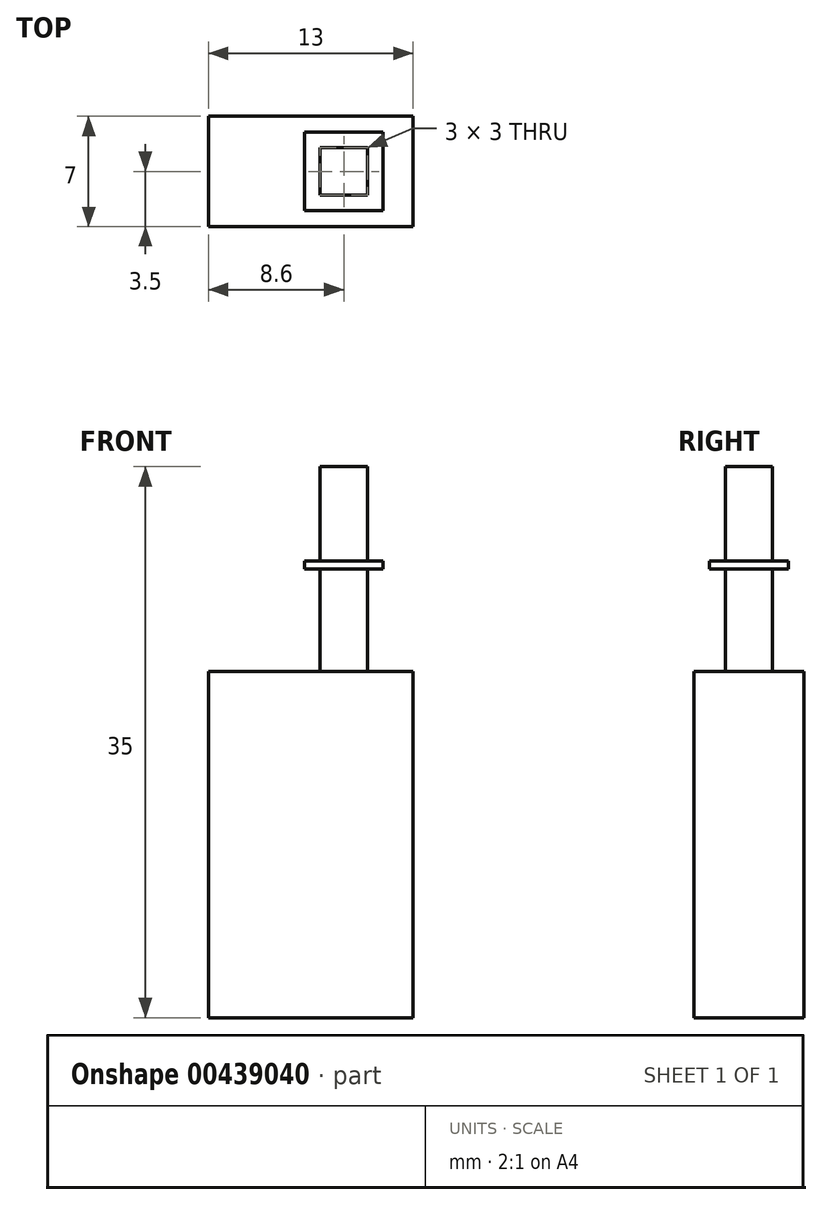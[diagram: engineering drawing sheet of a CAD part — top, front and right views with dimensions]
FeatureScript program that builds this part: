
annotation { "Feature Type Name" : "Feature", "Feature Type Description" : "" }
export const myFeature = defineFeature(function(context is Context, id is Id, definition is map)
    precondition{}
    {
        {
            var Q0;
            Q0=qCreatedBy(makeId("Top.planeOp"),FACE);
            var sketch = newSketch(context, id + "F0", { "sketchPlane" : qUnion([Q0])});
            skLineSegment(sketch, "E0.bottom", {"start": v(6.5, -3.5) * mm, "end": v(-6.5, -3.5) * mm});
            skLineSegment(sketch, "E0.top", {"start": v(6.5, 3.5) * mm, "end": v(-6.5, 3.5) * mm});
            skLineSegment(sketch, "E0.left", {"start": v(6.5, -3.5) * mm, "end": v(6.5, 3.5) * mm});
            skLineSegment(sketch, "E0.right", {"start": v(-6.5, -3.5) * mm, "end": v(-6.5, 3.5) * mm});
            skPoint(sketch, "E0.middle", {"position": v(0, 0) * mm});
            skSolve(sketch);
        }
        {
            var Q0;
            Q0=qSketchRegion(id+"F0",true);
            extrude(context, id + "F1", {"entities" : qUnion([Q0]), "depth" : 22 * mm});
        }
        {
            var Q0;
            Q0=makeQuery(id+"F1.opExtrude","CAP_FACE",FACE,{"disambiguationData":[OSD([sQuery(id+"F0.wireOp",EDGE,"E0.bottom"),sQuery(id+"F0.wireOp",EDGE,"E0.top"),sQuery(id+"F0.wireOp",EDGE,"E0.left"),sQuery(id+"F0.wireOp",EDGE,"E0.right")])],"isStart":false});
            var sketch = newSketch(context, id + "F2", { "sketchPlane" : qUnion([Q0])});
            skLineSegment(sketch, "E1.bottom", {"start": v(3.6, -1.5) * mm, "end": v(0.6, -1.5) * mm});
            skLineSegment(sketch, "E1.top", {"start": v(3.6, 1.5) * mm, "end": v(0.6, 1.5) * mm});
            skLineSegment(sketch, "E1.left", {"start": v(3.6, -1.5) * mm, "end": v(3.6, 1.5) * mm});
            skLineSegment(sketch, "E1.right", {"start": v(0.6, -1.5) * mm, "end": v(0.6, 1.5) * mm});
            skPoint(sketch, "E1.middle", {"position": v(2.1, 0) * mm});
            skSolve(sketch);
        }
        {
            var Q0;
            Q0=qSketchRegion(id+"F2",true);
            extrude(context, id + "F3", {"entities" : qUnion([Q0]), "depth" : 13 * mm});
        }
        {
            var Q0;
            Q0=makeQuery(id+"F3.opExtrude","CAP_FACE",FACE,{"disambiguationData":[OSD([sQuery(id+"F2.wireOp",EDGE,"E1.bottom"),sQuery(id+"F2.wireOp",EDGE,"E1.top"),sQuery(id+"F2.wireOp",EDGE,"E1.left"),sQuery(id+"F2.wireOp",EDGE,"E1.right")])],"isStart":false});
            cPlane(context, id + "F4", {"entities" : qUnion([Q0]), "cplaneType" : CPlaneType.OFFSET, "offset" : 6 * mm, "oppositeDirection" : true, "width" : 150 * mm, "height" : 150 * mm});
        }
        {
            var Q0;
            Q0=qCreatedBy(id+"F4.planeOp",FACE);
            var sketch = newSketch(context, id + "F5", { "sketchPlane" : qUnion([Q0])});
            skLineSegment(sketch, "E2.bottom", {"start": v(4.6, -2.5) * mm, "end": v(-0.4, -2.5) * mm});
            skLineSegment(sketch, "E2.top", {"start": v(4.6, 2.5) * mm, "end": v(-0.4, 2.5) * mm});
            skLineSegment(sketch, "E2.left", {"start": v(4.6, -2.5) * mm, "end": v(4.6, 2.5) * mm});
            skLineSegment(sketch, "E2.right", {"start": v(-0.4, -2.5) * mm, "end": v(-0.4, 2.5) * mm});
            skPoint(sketch, "E2.middle", {"position": v(2.1, 0) * mm});
            skSolve(sketch);
        }
        {
            var Q0;
            Q0=qSketchRegion(id+"F5",true);
            extrude(context, id + "F6", {"entities" : qUnion([Q0]), "operationType" : NewBodyOperationType.ADD, "oppositeDirection" : true, "depth" : 0.5 * mm});
        }
    });
